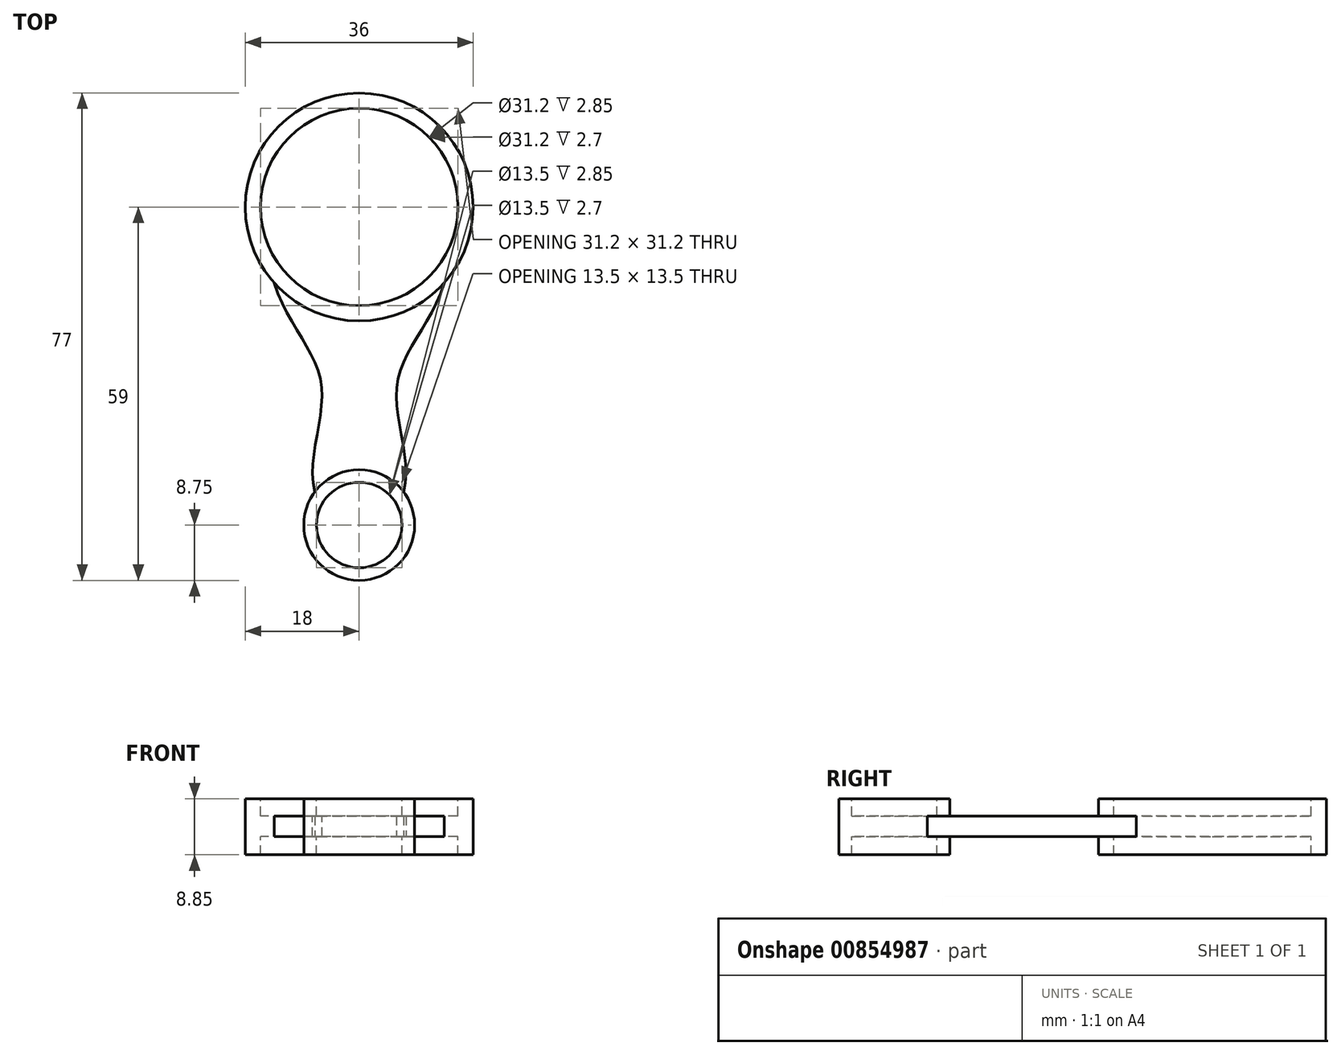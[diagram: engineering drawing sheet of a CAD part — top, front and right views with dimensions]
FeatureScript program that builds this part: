
annotation { "Feature Type Name" : "Feature", "Feature Type Description" : "" }
export const myFeature = defineFeature(function(context is Context, id is Id, definition is map)
    precondition{}
    {
        {
            var Q0;
            Q0=qCreatedBy(makeId("Top.planeOp"),FACE);
            var sketch = newSketch(context, id + "F0", { "sketchPlane" : qUnion([Q0])});
            skArc(sketch, "E0", {"start": v(13.42, 12) * mm, "mid": v(0, 42) * mm, "end": v(-13.42, 12) * mm});
            skArc(sketch, "E1", {"start": v(7.04, -21.05) * mm, "mid": v(0, -35) * mm, "end": v(-7.04, -21.05) * mm});
            skFitSpline(sketch, "E2", {"points": [v(7.04, -21.05) * mm, v(6, -3.92) * mm, v(13.42, 12) * mm], "startDerivative": vector(8.03, 32.59) * mm, "endDerivative": vector(11.86, 39.28) * mm});
            skFitSpline(sketch, "E3.MirrorCS", {"points": [v(-7.04, -21.05) * mm, v(-6, -3.92) * mm, v(-13.42, 12) * mm], "startDerivative": vector(-8.03, 32.59) * mm, "endDerivative": vector(-11.86, 39.28) * mm});
            skSolve(sketch);
        }
        {
            var Q0;
            Q0 = qSketchRegion(id + "F0", true);
            extrude(context, id + "F1", {"entities" : qUnion([Q0]), "depth" : 3.3 * mm, "offsetDistance" : 25 * mm});
        }
        {
            var Q0;
            Q0=makeQuery(id+"F1.opExtrude","CAP_FACE",FACE,{"disambiguationData":[OSD([sQuery(id+"F0.wireOp",EDGE,"E0"),sQuery(id+"F0.wireOp",EDGE,"E1"),sQuery(id+"F0.wireOp",EDGE,"E2"),sQuery(id+"F0.wireOp",EDGE,"E3.MirrorCS")])],"isStart":true});
            var sketch = newSketch(context, id + "F2", { "sketchPlane" : qUnion([Q0])});
            skCircle(sketch, "E4", {"center": v(0, -24) * mm, "radius": 18 * mm});
            skCircle(sketch, "E5", {"center": v(0, -24) * mm, "radius": 15.6 * mm});
            skCircle(sketch, "E6", {"center": v(0, 26.25) * mm, "radius": 8.75 * mm});
            skCircle(sketch, "E7", {"center": v(0, 26.25) * mm, "radius": 6.75 * mm});
            skSolve(sketch);
        }
        {
            var Q0;
            Q0 = qSketchRegion(id + "F2", true);
            extrude(context, id + "F3", {"entities" : qUnion([Q0]), "operationType" : NewBodyOperationType.ADD, "depth" : 2.85 * mm, "offsetDistance" : 25 * mm, "hasSecondDirection" : true, "secondDirectionOppositeDirection" : true, "secondDirectionDepth" : 6 * mm});
        }
    });
